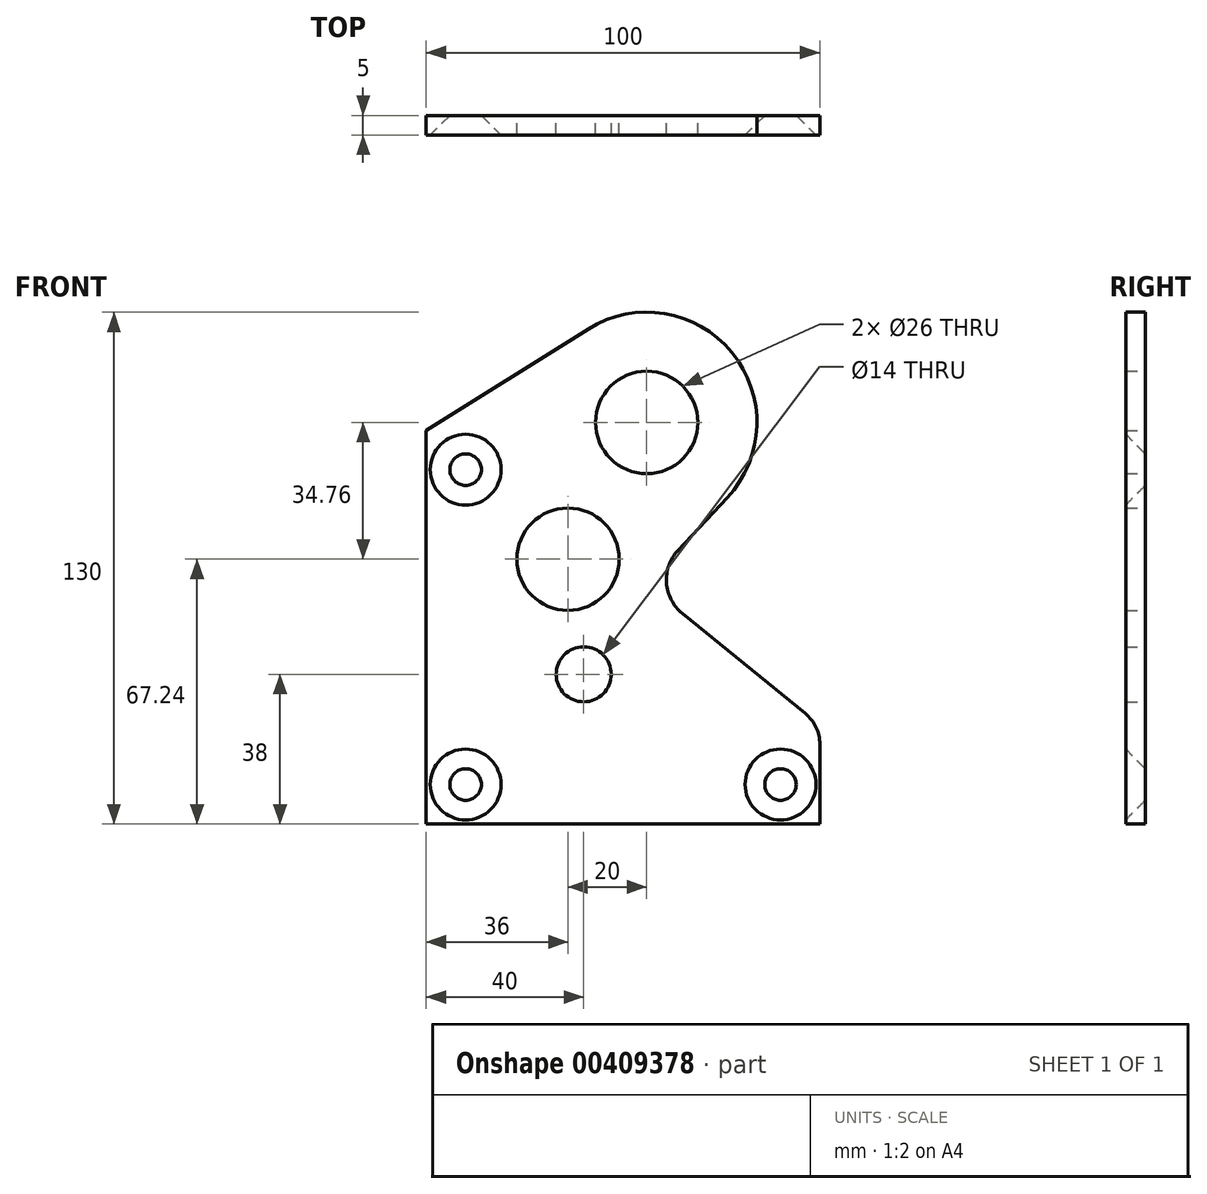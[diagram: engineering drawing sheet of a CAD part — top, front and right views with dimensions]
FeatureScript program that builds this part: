
annotation { "Feature Type Name" : "Feature", "Feature Type Description" : "" }
export const myFeature = defineFeature(function(context is Context, id is Id, definition is map)
    precondition{}
    {
        {
            var Q0;
            Q0=qCreatedBy(makeId("Front.planeOp"),FACE);
            var sketch = newSketch(context, id + "F0", { "sketchPlane" : qUnion([Q0])});
            skLineSegment(sketch, "E0", {"start": v(0, 0) * mm, "end": v(0, 100) * mm});
            skLineSegment(sketch, "E1", {"start": v(0, 0) * mm, "end": v(100, 0) * mm});
            skLineSegment(sketch, "E2", {"start": v(100, 0) * mm, "end": v(100, 25) * mm});
            skCircle(sketch, "E3", {"center": v(56, 102) * mm, "radius": 13 * mm});
            skArc(sketch, "E4", {"start": v(76.46, 82.88) * mm, "mid": v(77.61, 119.8) * mm, "end": v(41.15, 125.74) * mm});
            skLineSegment(sketch, "E5", {"start": v(0, 100) * mm, "end": v(41.15, 125.74) * mm});
            skArc(sketch, "E6", {"start": v(63.96, 69.51) * mm, "mid": v(61.03, 61.25) * mm, "end": v(65.05, 53.47) * mm});
            skLineSegment(sketch, "E7", {"start": v(100, 25) * mm, "end": v(65.05, 53.47) * mm});
            skLineSegment(sketch, "E8", {"start": v(63.96, 69.51) * mm, "end": v(76.46, 82.88) * mm});
            skCircle(sketch, "E9", {"center": v(90, 10) * mm, "radius": 4 * mm});
            skCircle(sketch, "E10", {"center": v(10, 10) * mm, "radius": 4 * mm});
            skCircle(sketch, "E11", {"center": v(10, 90) * mm, "radius": 4 * mm});
            skCircle(sketch, "E12", {"center": v(36, 67.24) * mm, "radius": 13 * mm});
            skCircle(sketch, "E13", {"center": v(40, 38) * mm, "radius": 7 * mm});
            skSolve(sketch);
        }
        {
            var Q0;
            Q0=makeQuery(id+"F0.imprint","IMPRINT",FACE,{"disambiguationData":[TD([[makeQuery(id+"F0.imprint","IMPRINT",EDGE,{"derivedFrom":sQuery(id+"F0.wireOp",EDGE,"E0")}),-1.0]])]});
            extrude(context, id + "F1", {"entities" : qUnion([Q0]), "depth" : 5 * mm});
        }
        {
            var Q0;
            Q0=makeQuery(id+"F1.opExtrude","CAP_EDGE",EDGE,{"disambiguationData":[OSD([sQuery(id+"F0.wireOp",EDGE,"E10")])],"isStart":false});
            var Q1;
            Q1=makeQuery(id+"F1.opExtrude","CAP_EDGE",EDGE,{"disambiguationData":[OSD([sQuery(id+"F0.wireOp",EDGE,"E9")])],"isStart":false});
            var Q2;
            Q2=makeQuery(id+"F1.opExtrude","CAP_EDGE",EDGE,{"disambiguationData":[OSD([sQuery(id+"F0.wireOp",EDGE,"E11")])],"isStart":false});
            chamfer(context, id + "F2", {"entities" : qUnion([Q0, Q1, Q2]), "width" : 5 * mm, "tangentPropagation" : true});
        }
        {
            var Q0;
            Q0=makeQuery(id+"F1.opExtrude","SWEPT_EDGE",EDGE,{"disambiguationData":[OSD([sQuery(id+"F0.wireOp",EDGE,"E2"),sQuery(id+"F0.wireOp",EDGE,"E7")])]});
            fillet(context, id + "F3", {"entities" : qUnion([Q0]), "radius" : 10 * mm, "tangentPropagation" : true, "allowEdgeOverflow" : false});
        }
    });
